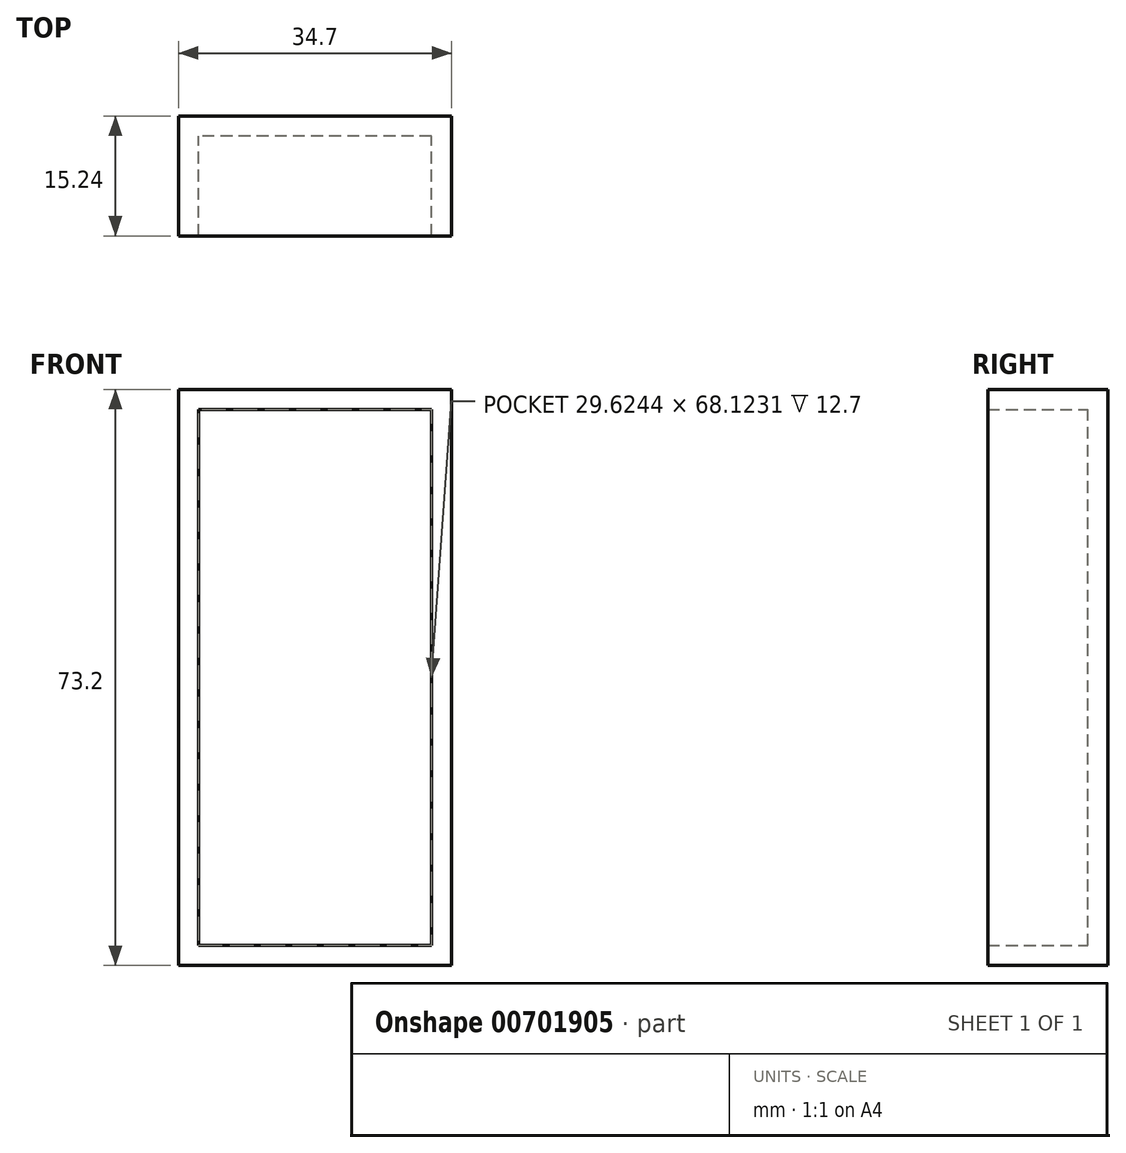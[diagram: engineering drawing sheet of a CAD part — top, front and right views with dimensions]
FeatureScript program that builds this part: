
annotation { "Feature Type Name" : "Feature", "Feature Type Description" : "" }
export const myFeature = defineFeature(function(context is Context, id is Id, definition is map)
    precondition{}
    {
        {
            var Q0;
            Q0=qCreatedBy(makeId("Front.planeOp"),FACE);
            var sketch = newSketch(context, id + "F0", { "sketchPlane" : qUnion([Q0])});
            skLineSegment(sketch, "E0.bottom", {"start": v(0, 0) * mm, "end": v(-29.62, 0) * mm});
            skLineSegment(sketch, "E0.top", {"start": v(0, 68.12) * mm, "end": v(-29.62, 68.12) * mm});
            skLineSegment(sketch, "E0.left", {"start": v(0, 0) * mm, "end": v(0, 68.12) * mm});
            skLineSegment(sketch, "E0.right", {"start": v(-29.62, 0) * mm, "end": v(-29.62, 68.12) * mm});
            skSolve(sketch);
        }
        {
            var Q0;
            Q0=makeQuery(id+"F0.imprint","IMPRINT",FACE,{"disambiguationData":[TD([[makeQuery(id+"F0.imprint","IMPRINT",EDGE,{"derivedFrom":sQuery(id+"F0.wireOp",EDGE,"E0.bottom")}),-1.0]])]});
            extrude(context, id + "F1", {"entities" : qUnion([Q0]), "depth" : 12.7 * mm, "offsetDistance" : 25.4 * mm});
        }
        {
            var Q0;
            Q0=makeQuery(id+"F1.opExtrude","CAP_FACE",FACE,{"disambiguationData":[OSD([sQuery(id+"F0.wireOp",EDGE,"E0.bottom"),sQuery(id+"F0.wireOp",EDGE,"E0.top"),sQuery(id+"F0.wireOp",EDGE,"E0.left"),sQuery(id+"F0.wireOp",EDGE,"E0.right")])],"isStart":false});
            shell(context, id + "F2", {"entities" : qUnion([Q0]), "thickness" : 2.54 * mm, "oppositeDirection" : true});
        }
    });
